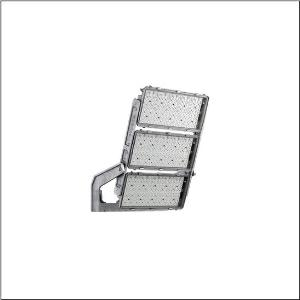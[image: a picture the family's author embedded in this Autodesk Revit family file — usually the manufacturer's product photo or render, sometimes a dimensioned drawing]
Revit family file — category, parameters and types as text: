
# Revit family: floodlight_fl_11_maxi_pro_remote___pl43_5xa779524a01aa_32ee
name_source: partatom
category: Lighting Fixtures
units: mm (PartAtom-declared; Revit-internal decimal feet)

## family parameters
Cut with Voids When Loaded = No
Host = Face
Light Source = No
Part Type = Normal
Room Calculation Point = No
Round Connector Dimension = Use Diameter
Shared = No

## types (1)
- --- (1 x LED, 130000 lm, 1334.7 W, 5700K)
    Apparent Load = 1335 VA
    CIE Flux Codes = 25 74 99 100 100
    Color Rendering = 90
    Color Temperature = 5700K
    Default Elevation = 1800 mm
    Description = Floodlight FL 11  maxi  pro Remote floodlight; light control with lens of PMMA; cover panel of toughened safety glass, transparent; light distribution: PL43, asymmetric direct distribution, LEDcolour temperature: 5700K, rated luminous flux: 130.000lm, colour rendering: CRI > 90, light colour: 957; luminous efficacy: 97lm/W; brightness control: DMX+RDM; with terminal, 8-pole, max. 2.5mm², mains connection: 220..240V/380..400V AC, 50/60Hz, surge voltage resistance: line to ground: 10kV, ECG replaceable separately, no afterglow with DALI off / DMX off command, LED unit replaceable without ESD environment, dustproof LED module, dimming range 10..100%; 1335W floodlight with 3x LED unit of diecast aluminium, coated grey; length: 713mm / width: 651mm / height: 338mm; mounting bracket, of diecast aluminium, uncoated, natural, equipment: Power, protection rating (complete): IP66; insulation class (complete): insulation class I (protective earthing); certification: CE, ENEC, VDE; ball protection: ball impact resistance with accessories, impact resistance: IK07; only for outdoor installations, rated ambient temperature 10°C, permissible operating ambient temperature: -40..+30°C, permissible storage temperature: -40..+85°C; packaging unit: 1 piece

Light Distribution: PL43
    Height = 320 mm
    Lamp = 1 x LED
    Lamp Light Flux = 130000 lm
    Lamp Power = 1334.7 W
    Lamp count = 1
    Length = 1002 mm
    Luminous efficacy = 97 lm/W
    Manufacturer = Siteco
    ModVariant = No
    Model = 5XA779524A01AA
    Mounting Place = Ceiling
    Mounting Type = Surface mounted
    Number of Poles = 1
    OnlyDefault = Yes
    Power Factor = 1
    Product Name = Floodlight FL 11 maxi pro Remote | PL43
    Product group = floodlight | ceiling mounted
    ProductGroupID = 303
    Protection Class = Protection class I
    Protection Degree = IP 66
    RLX_Detail_Level = 1
    RLX_Emergency_Light_Flux = 0 lm
    RLX_Emergency_Type = 0
    RLX_Emergency_Type_DB = No
    RlxData = <blob elided: 52309 chars, md5=4439b64a>
    Socket = socket
    Standby Power = 0 W
    System Light Flux = 130000 lm
    System Power = 1335 W
    Type Comments = factory setting: luminous flux: 100 % | dim-lin: 255 | 920 mA
    Type Image = l_1006784.jpg
    URL = http://relux.com
    VarID = @adj_045215
    Voltage = 0 V
    Weight = 0.00 kg
    Width = 655 mm

## geometry (parser evidence)
native form markers: Blend x4, Sweep x13
no freeform markers — native parametric forms only
